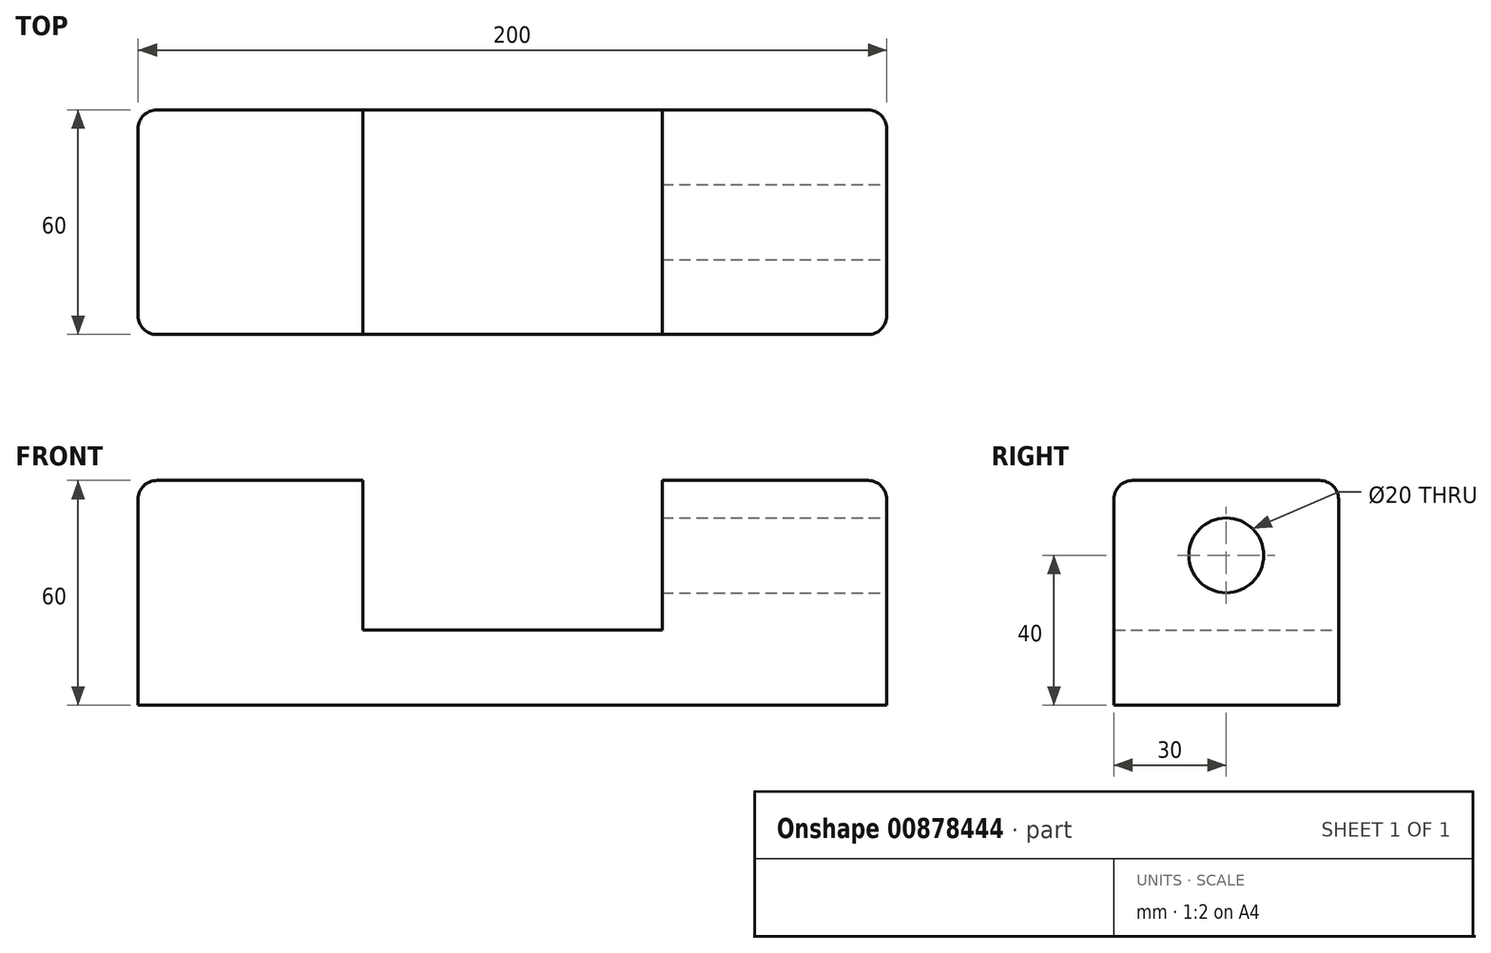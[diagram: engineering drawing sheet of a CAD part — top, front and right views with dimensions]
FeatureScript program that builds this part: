
annotation { "Feature Type Name" : "Feature", "Feature Type Description" : "" }
export const myFeature = defineFeature(function(context is Context, id is Id, definition is map)
    precondition{}
    {
        {
            var Q0;
            Q0=qCreatedBy(makeId("Front.planeOp"),FACE);
            var sketch = newSketch(context, id + "F0", { "sketchPlane" : qUnion([Q0])});
            skLineSegment(sketch, "E0.bottom", {"start": v(100, -30) * mm, "end": v(-100, -30) * mm});
            skLineSegment(sketch, "E0.left", {"start": v(100, -30) * mm, "end": v(100, 30) * mm});
            skLineSegment(sketch, "E0.right", {"start": v(-100, -30) * mm, "end": v(-100, 30) * mm});
            skPoint(sketch, "E0.middle", {"position": v(0, 0) * mm});
            skLineSegment(sketch, "E1", {"start": v(-100, 30) * mm, "end": v(-40, 30) * mm});
            skLineSegment(sketch, "E2", {"start": v(-40, 30) * mm, "end": v(-40, -10) * mm});
            skLineSegment(sketch, "E3", {"start": v(-40, -10) * mm, "end": v(40, -10) * mm});
            skLineSegment(sketch, "E4", {"start": v(40, -10) * mm, "end": v(40, 30) * mm});
            skLineSegment(sketch, "E5", {"start": v(40, 30) * mm, "end": v(100, 30) * mm});
            skSolve(sketch);
        }
        {
            var Q0;
            Q0=makeQuery(id+"F0.imprint","IMPRINT",FACE,{"disambiguationData":[TD([[makeQuery(id+"F0.imprint","IMPRINT",EDGE,{"derivedFrom":sQuery(id+"F0.wireOp",EDGE,"E0.bottom")}),-1.0]])]});
            extrude(context, id + "F1", {"entities" : qUnion([Q0]), "depth" : 60 * mm, "offsetDistance" : 25 * mm});
        }
        {
            var Q0;
            Q0=makeQuery(id+"F1.opExtrude","SWEPT_FACE",FACE,{"disambiguationData":[OSD([sQuery(id+"F0.wireOp",EDGE,"E0.left")])]});
            var sketch = newSketch(context, id + "F2", { "sketchPlane" : qUnion([Q0])});
            skLineSegment(sketch, "E6", {"start": v(-30, 30) * mm, "end": v(-30, 10) * mm});
            skCircle(sketch, "E7", {"center": v(-30, 10) * mm, "radius": 10 * mm});
            skSolve(sketch);
        }
        {
            var Q0;
            Q0=makeQuery(id+"F2.imprint","IMPRINT",FACE,{"disambiguationData":[TD([[makeQuery(id+"F2.imprint","IMPRINT",EDGE,{"derivedFrom":sQuery(id+"F2.wireOp",EDGE,"E7")}),1.0]])]});
            extrude(context, id + "F3", {"entities" : qUnion([Q0]), "operationType" : NewBodyOperationType.REMOVE, "oppositeDirection" : true, "depth" : 60 * mm, "offsetDistance" : 25 * mm});
        }
        {
            var Q0;
            Q0=makeQuery(id+"F1.opExtrude","CAP_EDGE",EDGE,{"disambiguationData":[OSD([sQuery(id+"F0.wireOp",EDGE,"E5")])],"isStart":false});
            var Q1;
            Q1=makeQuery(id+"F1.opExtrude","CAP_EDGE",EDGE,{"disambiguationData":[OSD([sQuery(id+"F0.wireOp",EDGE,"E5")])],"isStart":true});
            var Q2;
            Q2=makeQuery(id+"F1.opExtrude","SWEPT_EDGE",EDGE,{"disambiguationData":[OSD([sQuery(id+"F0.wireOp",EDGE,"E0.left"),sQuery(id+"F0.wireOp",EDGE,"E5")])]});
            var Q3;
            Q3=makeQuery(id+"F1.opExtrude","CAP_EDGE",EDGE,{"disambiguationData":[OSD([sQuery(id+"F0.wireOp",EDGE,"E1")])],"isStart":false});
            var Q4;
            Q4=makeQuery(id+"F1.opExtrude","CAP_EDGE",EDGE,{"disambiguationData":[OSD([sQuery(id+"F0.wireOp",EDGE,"E1")])],"isStart":true});
            var Q5;
            Q5=makeQuery(id+"F1.opExtrude","SWEPT_EDGE",EDGE,{"disambiguationData":[OSD([sQuery(id+"F0.wireOp",EDGE,"E0.right"),sQuery(id+"F0.wireOp",EDGE,"E1")])]});
            var Q6;
            Q6=makeQuery(id+"F1.opExtrude","CAP_EDGE",EDGE,{"disambiguationData":[OSD([sQuery(id+"F0.wireOp",EDGE,"E0.left")])],"isStart":true});
            var Q7;
            Q7=makeQuery(id+"F1.opExtrude","CAP_EDGE",EDGE,{"disambiguationData":[OSD([sQuery(id+"F0.wireOp",EDGE,"E0.left")])],"isStart":false});
            var Q8;
            Q8=makeQuery(id+"F1.opExtrude","CAP_EDGE",EDGE,{"disambiguationData":[OSD([sQuery(id+"F0.wireOp",EDGE,"E0.right")])],"isStart":true});
            var Q9;
            Q9=makeQuery(id+"F1.opExtrude","CAP_EDGE",EDGE,{"disambiguationData":[OSD([sQuery(id+"F0.wireOp",EDGE,"E0.right")])],"isStart":false});
            fillet(context, id + "F4", {"entities" : qUnion([Q0, Q1, Q2, Q3, Q4, Q5, Q6, Q7, Q8, Q9]), "radius" : 5 * mm, "tangentPropagation" : true, "allowEdgeOverflow" : false});
        }
    });
